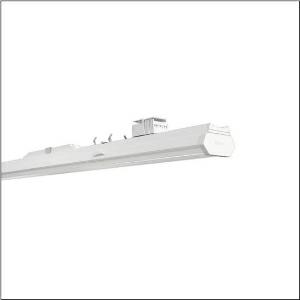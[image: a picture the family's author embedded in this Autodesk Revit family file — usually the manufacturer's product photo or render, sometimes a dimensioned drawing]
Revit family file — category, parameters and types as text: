
# Revit family: licross_r__21_protected_ho_52td1bcn4b5m_1c3e
name_source: partatom
category: Lighting Fixtures
units: mm (PartAtom-declared; Revit-internal decimal feet)

## family parameters
Cut with Voids When Loaded = No
Host = Face
Light Source = No
Part Type = Normal
Room Calculation Point = No
Round Connector Dimension = Use Diameter
Shared = No

## types (1)
- --- (1 x LED, 11820 lm, 68.9 W, 4000K)
    Apparent Load = 69 VA
    CIE Flux Codes = 54 82 95 97 100
    Color Rendering = 80
    Color Temperature = 4000K
    Default Elevation = 1800 mm
    Description = Licross® 21 Protected HO, luminaire insert, of sheet steel, galvanised, coil coated, white, length: 1.500mm, width: 90mm, height: 103mm, LED rated luminous flux: 11.830lm, light colour: 840, control gear: ON/OFF Multilumen, CLOi, control gear: ECG Multilumen, with plug, 3-pole, with phase selection, mains connection: 220..240V, AC, 50/60Hz, start of lifetime: 69W, end of service life: 83W, halogen-free wiring, primary optical cover: cover, of PMMA, light emission: direct distribution, primary light characteristic: symmetric, protection rating (complete): IP54, insulation class (complete): insulation class I (protective earthing), certification: CE, ENEC, VDE, UKCA, protection symbol: D if used in an environment with non-conductive dust loads with corresponding accessories, impact resistance: IK06, permissible ambient temperature for indoor applications: -35..+35°C, corresponds to IFS (International Featured Standards) requirements for safety and quality in the food industry, reducing of maximum allowable ambient temperature of 5°C with ceiling mounting, LABS conformity tested according to VDMA 24364:2018-05, packaging unit: 1 piece
    Height = 92 mm
    Lamp = 1 x LED
    Lamp Light Flux = 11820 lm
    Lamp Power = 68.9 W
    Lamp count = 1
    Length = 1500 mm
    Luminous efficacy = 172 lm/W
    Manufacturer = Siteco
    ModVariant = No
    Model = 52TD1BCN4B5M
    Mounting Place = Ceiling
    Mounting Type = Pendant
    Number of Poles = 1
    OnlyDefault = Yes
    Power Factor = 1
    Product Name = Licross® 21 Protected HO
    Product group = luminaire insert
    ProductGroupID = 902
    Protection Class = Protection class I
    Protection Degree = IP 54
    RLX_Detail_Level = 1
    RLX_Emergency_Light_Flux = 0 lm
    RLX_Emergency_Type = 0
    RLX_Emergency_Type_DB = No
    RlxData = <blob elided: 22065 chars, md5=a88f7e72>
    Socket = socket
    Standby Power = 0 W
    System Light Flux = 11820 lm
    System Power = 69 W
    Type Comments = factory setting: luminous flux: 100 % | (A | C | E) | 162 mA
    Type Image = l_1256148.jpg
    URL = http://relux.com
    VarID = @adj_111534
    Voltage = 0 V
    Weight = 0.00 kg
    Width = 88 mm

## geometry (parser evidence)
native form markers: Blend x4, Sweep x13
no freeform markers — native parametric forms only
